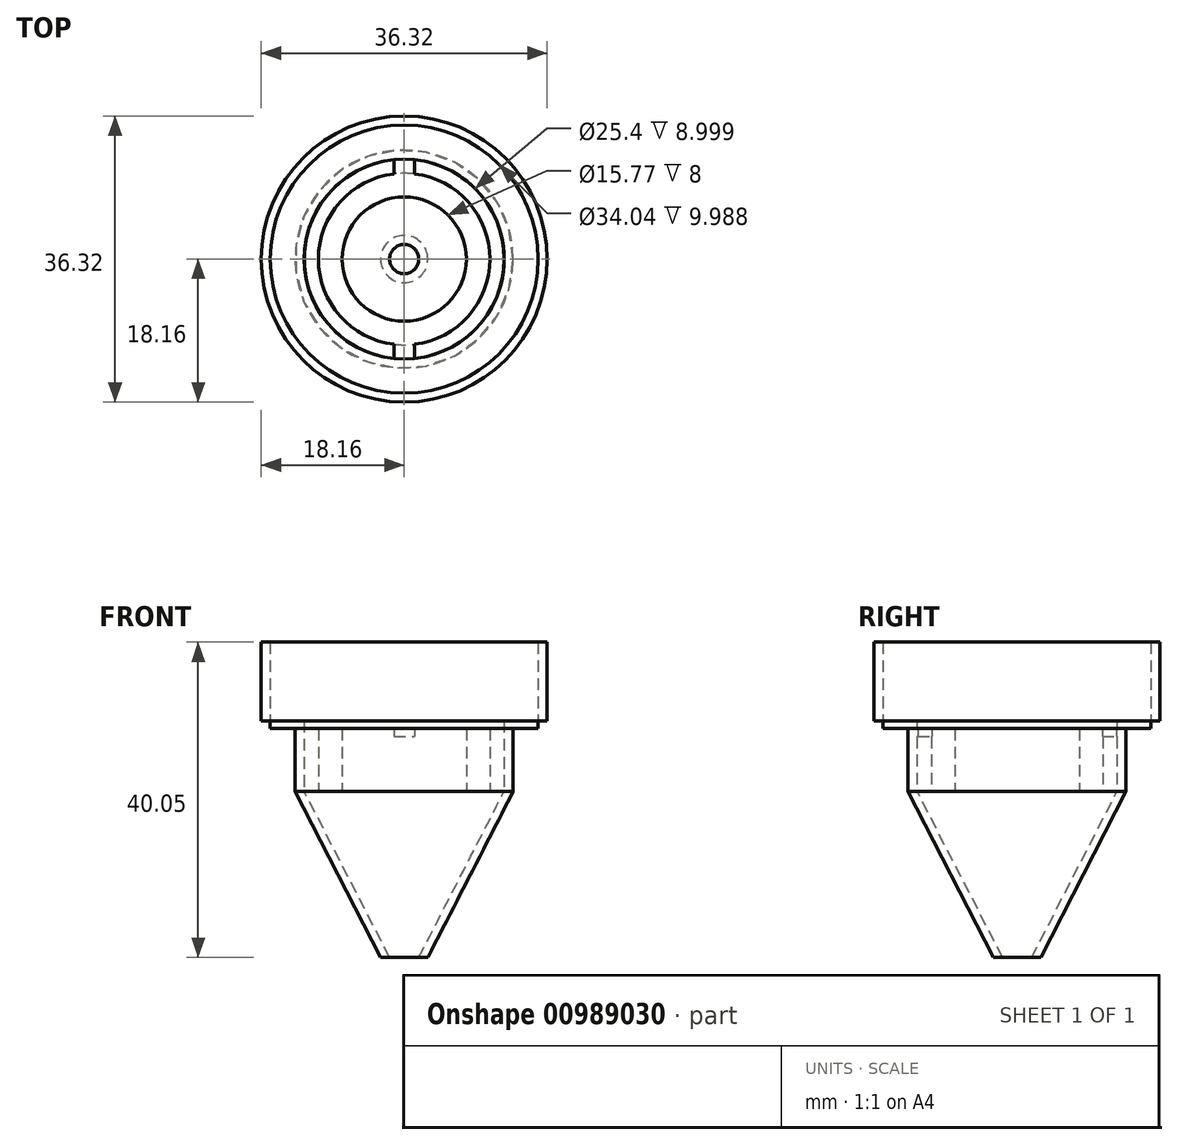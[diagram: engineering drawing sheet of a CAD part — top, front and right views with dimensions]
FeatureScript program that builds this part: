
annotation { "Feature Type Name" : "Feature", "Feature Type Description" : "" }
export const myFeature = defineFeature(function(context is Context, id is Id, definition is map)
    precondition{}
    {
        {
            var Q0;
            Q0=qCreatedBy(makeId("Top.planeOp"),FACE);
            var sketch = newSketch(context, id + "F0", { "sketchPlane" : qUnion([Q0])});
            skCircle(sketch, "E0", {"center": v(0, 0) * mm, "radius": 7.89 * mm});
            skArc(sketch, "E1", {"start": v(1.3, -10.82) * mm, "mid": v(10.9, 0) * mm, "end": v(1.3, 10.82) * mm});
            skArc(sketch, "E2", {"start": v(1.3, -12.63) * mm, "mid": v(12.7, 0) * mm, "end": v(1.3, 12.63) * mm});
            skCircle(sketch, "E3", {"center": v(0, 0) * mm, "radius": 13.84 * mm});
            skLineSegment(sketch, "E4", {"start": v(-1.3, -12.63) * mm, "end": v(-1.3, -10.82) * mm});
            skLineSegment(sketch, "E5.MirrorCS", {"start": v(1.3, -12.63) * mm, "end": v(1.3, -10.82) * mm});
            skLineSegment(sketch, "E6.trimOffspring", {"start": v(-1.3, 10.82) * mm, "end": v(-1.3, 12.63) * mm});
            skLineSegment(sketch, "E7.trimOffspring", {"start": v(1.3, 10.82) * mm, "end": v(1.3, 12.63) * mm});
            skArc(sketch, "E8.trimOffspring", {"start": v(-1.3, 10.82) * mm, "mid": v(-10.9, 0) * mm, "end": v(-1.3, -10.82) * mm});
            skArc(sketch, "E9.trimOffspring", {"start": v(-1.3, 12.63) * mm, "mid": v(-12.7, 0) * mm, "end": v(-1.3, -12.63) * mm});
            skSolve(sketch);
        }
        {
            var Q0;
            Q0 = qSketchRegion(id + "F0", true);
            extrude(context, id + "F1", {"entities" : qUnion([Q0]), "depth" : 8 * mm, "offsetDistance" : 25.4 * mm});
        }
        {
            var Q0;
            Q0=qCreatedBy(makeId("Top.planeOp"),FACE);
            var sketch = newSketch(context, id + "F2", { "sketchPlane" : qUnion([Q0])});
            skCircle(sketch, "E10", {"center": v(0, 0) * mm, "radius": 12.7 * mm});
            skCircle(sketch, "E11", {"center": v(0, 0) * mm, "radius": 10.9 * mm});
            skSolve(sketch);
        }
        {
            var Q0;
            Q0 = qSketchRegion(id + "F2", true);
            extrude(context, id + "F3", {"entities" : qUnion([Q0]), "depth" : 7 * mm, "offsetDistance" : 25.4 * mm});
        }
        {
            var Q0;
            Q0=makeQuery(id+"F3.opExtrude","SWEPT_BODY",BODY,{"disambiguationData":[OSD([sQuery(id+"F2.wireOp",EDGE,"E10"),sQuery(id+"F2.wireOp",EDGE,"E11")])]});
            var Q1;
            Q1=makeQuery(id+"F1.opExtrude","SWEPT_BODY",BODY,{"disambiguationData":[OSD([sQuery(id+"F0.wireOp",EDGE,"E0"),sQuery(id+"F0.wireOp",EDGE,"E1"),sQuery(id+"F0.wireOp",EDGE,"E2"),sQuery(id+"F0.wireOp",EDGE,"E3"),sQuery(id+"F0.wireOp",EDGE,"E4"),sQuery(id+"F0.wireOp",EDGE,"E5.MirrorCS"),sQuery(id+"F0.wireOp",EDGE,"E6.trimOffspring"),sQuery(id+"F0.wireOp",EDGE,"E7.trimOffspring"),sQuery(id+"F0.wireOp",EDGE,"E8.trimOffspring"),sQuery(id+"F0.wireOp",EDGE,"E9.trimOffspring")])]});
            booleanBodies(context, id + "F4", {"operationType" : BooleanOperationType.SUBTRACTION, "tools" : qUnion([Q0]), "targets" : qUnion([Q1])});
        }
        {
            var Q0;
            Q0=qCreatedBy(makeId("Top.planeOp"),FACE);
            cPlane(context, id + "F5", {"entities" : qUnion([Q0]), "cplaneType" : CPlaneType.OFFSET, "offset" : 8 * mm, "width" : 152.4 * mm, "height" : 152.4 * mm});
        }
        {
            var Q0;
            Q0=qCreatedBy(id+"F5.planeOp",FACE);
            var sketch = newSketch(context, id + "F6", { "sketchPlane" : qUnion([Q0])});
            skCircle(sketch, "E12", {"center": v(0, 0) * mm, "radius": 17.02 * mm});
            skCircle(sketch, "E13", {"center": v(0, 0) * mm, "radius": 12.7 * mm});
            skSolve(sketch);
        }
        {
            var Q0;
            Q0 = qSketchRegion(id + "F6", true);
            extrude(context, id + "F7", {"entities" : qUnion([Q0]), "operationType" : NewBodyOperationType.ADD, "depth" : 1 * mm, "offsetDistance" : 25.4 * mm});
        }
        {
            var Q0;
            Q0=qCreatedBy(makeId("Top.planeOp"),FACE);
            cPlane(context, id + "F8", {"entities" : qUnion([Q0]), "cplaneType" : CPlaneType.OFFSET, "offset" : 9 * mm, "width" : 152.4 * mm, "height" : 152.4 * mm});
        }
        {
            var Q0;
            Q0=qCreatedBy(id+"F8.planeOp",FACE);
            var sketch = newSketch(context, id + "F9", { "sketchPlane" : qUnion([Q0])});
            skCircle(sketch, "E14", {"center": v(0, 0) * mm, "radius": 18.16 * mm});
            skCircle(sketch, "E15", {"center": v(0, 0) * mm, "radius": 17.02 * mm});
            skSolve(sketch);
        }
        {
            var Q0;
            Q0=qCreatedBy(makeId("Front.planeOp"),FACE);
            var sketch = newSketch(context, id + "F10", { "sketchPlane" : qUnion([Q0])});
            skLineSegment(sketch, "E16", {"start": v(-13.84, 0) * mm, "end": v(-3, -21.06) * mm});
            skLineSegment(sketch, "E17", {"start": v(0, 0) * mm, "end": v(0, -21.06) * mm});
            skLineSegment(sketch, "E18", {"start": v(-3, -21.06) * mm, "end": v(-1.85, -21.06) * mm});
            skLineSegment(sketch, "E19", {"start": v(-13.84, 0) * mm, "end": v(-12.7, 0) * mm});
            skLineSegment(sketch, "E20", {"start": v(-12.7, 0) * mm, "end": v(-1.85, -21.06) * mm});
            skSolve(sketch);
        }
        {
            var Q0;
            Q0=makeQuery(id+"F10.imprint","IMPRINT",FACE,{"disambiguationData":[TD([[makeQuery(id+"F10.imprint","IMPRINT",EDGE,{"derivedFrom":sQuery(id+"F10.wireOp",EDGE,"E16")}),1.0]])]});
            var Q1;
            Q1=sQuery(id+"F10.wireOp",EDGE,"E17");
            revolve(context, id + "F11", {"operationType" : NewBodyOperationType.ADD, "surfaceOperationType" : NewSurfaceOperationType.NEW, "entities" : qUnion([Q0]), "axis" : qUnion([Q1]), "revolveType" : RevolveType.FULL});
        }
        {
            var Q0;
            Q0 = qSketchRegion(id + "F9", true);
            extrude(context, id + "F12", {"entities" : qUnion([Q0]), "operationType" : NewBodyOperationType.ADD, "depth" : 10 * mm, "offsetDistance" : 25.4 * mm});
        }
    });
